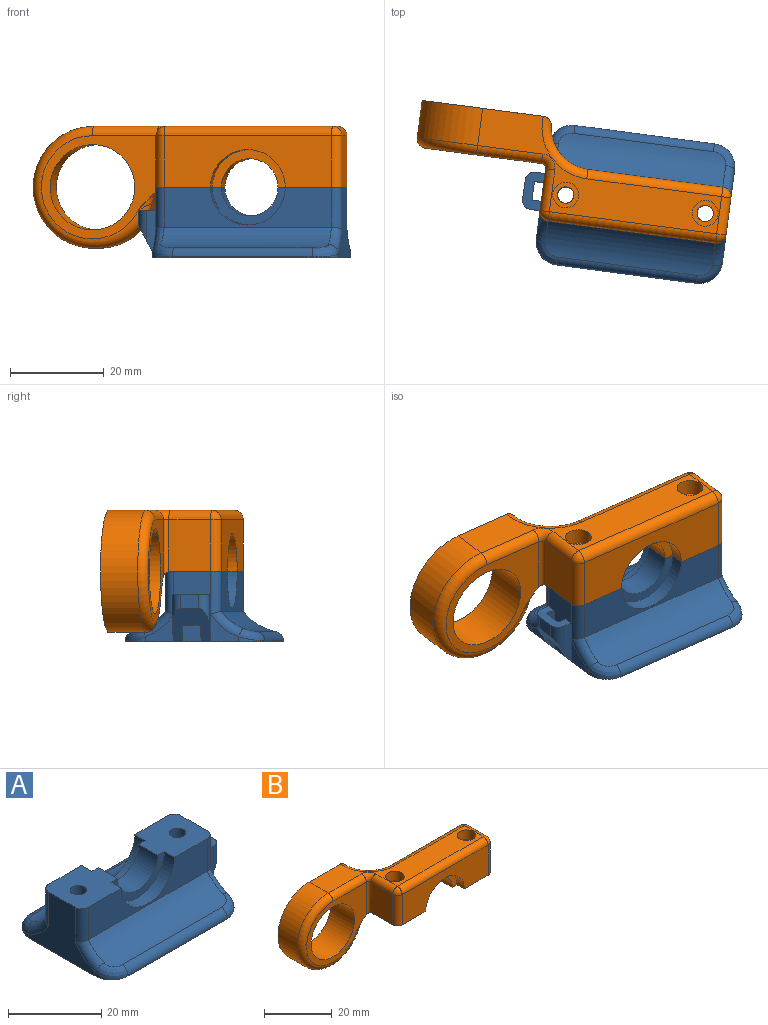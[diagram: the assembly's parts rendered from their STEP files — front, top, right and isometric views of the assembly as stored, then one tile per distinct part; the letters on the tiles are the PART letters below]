
ASSEMBLY  parts=2 mates=1
PART A: 48 faces, bbox 44.1x30x16.5 mm
  f0: plane 10x2mm, normal (0,-1,0), area 16.5mm2, adj f6,f25,f44,f45,f46
  f1: plane 10x2mm, normal (0,-1,0), area 16.5mm2, adj f2,f5,f44,f45
  f2: plane 6.5x4mm, normal (-1,0,0), area 26mm2, adj f1,f3,f44,f45
  f3: plane 10x2mm, normal (0,1,0), area 16.5mm2, adj f2,f5,f44,f45
  f4: plane 10x2mm, normal (0,1,0), area 16.5mm2, adj f7,f32,f44,f45,f47
  f5: plane 15x8mm, normal (1,0,0), area 80mm2, adj f1,f3,f10,f11,f25,f32,f44
  f6: plane 6x5.86mm, normal (1,0,0), area 17.5mm2, adj f0,f10,f24,f26
  f7: plane 6x5.86mm, normal (1,0,0), area 17.5mm2, adj f4,f10,f22,f33
  f8: cylinder r=6.1mm len=12.2mm, axis (0,1,0), area 111.1mm2, adj f11,f12,f40,f42
  f9: plane 36x8.5mm, normal (0,1,0), area 204.2mm2, adj f11,f12,f16,f32,f35,f39
  f10: plane 40x30mm, normal (0,0,-1), area 1159.3mm2, adj f5,f6,f7,f13,f14,f15,f19,f20
  f11: plane 13.9x12mm, normal (0,0,1), area 143.4mm2, adj f5,f8,f9,f18,f20,f25,f32,f39
  f12: plane 13.9x12mm, normal (0,0,1), area 143.4mm2, adj f8,f9,f13,f18,f19,f27,f35,f39
  f13: plane 20x15mm, normal (-1,0,0), area 155.1mm2, adj f10,f12,f21,f23,f27,f29,f35,f37
  f14: plane 30x0.15mm, normal (0,-1,0), area 4.6mm2, adj f10,f23,f24,f30
  f15: plane 30x0.15mm, normal (0,1,0), area 4.6mm2, adj f10,f21,f22,f36
  f16: cylinder r=11.25mm len=36mm, axis (1,0,0), area 310.8mm2, adj f9,f33,f34,f36,f37,f38
  f17: cylinder r=11.25mm len=36mm, axis (1,0,0), area 310.8mm2, adj f18,f26,f28,f29,f30,f31
  f18: plane 36x8.5mm, normal (0,-1,0), area 204.2mm2, adj f11,f12,f17,f25,f27,f41
  f19: cylinder r=1.75mm len=15mm, axis (0,0,-1), area 164.9mm2, adj f10,f12
  f20: cylinder r=1.75mm len=15mm, axis (0,0,-1), area 164.9mm2, adj f10,f11
  f21: cylinder r=5mm len=5mm, axis (0,0,-1), area 3.1mm2, adj f10,f13,f15,f38
  f22: cylinder r=5mm len=5mm, axis (0,0,1), area 3.1mm2, adj f7,f10,f15,f34
  f23: cylinder r=5mm len=5mm, axis (0,0,1), area 3.1mm2, adj f10,f13,f14,f31
  f24: cylinder r=5mm len=5mm, axis (0,0,-1), area 3.1mm2, adj f6,f10,f14,f28
  f25: cylinder r=2mm len=9.14mm, axis (0,0,-1), area 27.4mm2, adj f0,f5,f11,f18,f26
  f26: torus R=13.25mm, axis (1,0,0), area 21.1mm2, adj f6,f17,f25,f28
  f27: cylinder r=2mm len=9.14mm, axis (0,0,1), area 27.4mm2, adj f12,f13,f18,f29
  f28: bspline ~6.22x5.36mm, area 18.7mm2, adj f17,f24,f26,f30
  f29: torus R=13.25mm, axis (1,0,0), area 21.1mm2, adj f13,f17,f27,f31
  f30: cylinder r=2mm len=30mm, axis (1,0,0), area 85.2mm2, adj f14,f17,f28,f31
  f31: bspline ~6.22x6.18mm, area 18.7mm2, adj f17,f23,f29,f30
  f32: cylinder r=2mm len=9.14mm, axis (0,0,1), area 27.4mm2, adj f4,f5,f9,f11,f33
  f33: torus R=13.25mm, axis (1,0,0), area 21.1mm2, adj f7,f16,f32,f34
  f34: bspline ~6.22x6.18mm, area 18.7mm2, adj f16,f22,f33,f36
  f35: cylinder r=2mm len=9.14mm, axis (0,0,-1), area 27.4mm2, adj f9,f12,f13,f37
  f36: cylinder r=2mm len=30mm, axis (1,0,0), area 85.2mm2, adj f15,f16,f34,f38
  f37: torus R=13.25mm, axis (1,0,0), area 21.1mm2, adj f13,f16,f35,f38
  f38: bspline ~6.22x6.18mm, area 18.7mm2, adj f16,f21,f36,f37
  f39: cylinder r=8.05mm len=16.1mm, axis (0,1,0), area 78.4mm2, adj f9,f11,f12,f40
  f40: plane 16.1x8.05mm, normal (0,1,0), area 43.3mm2, adj f8,f11,f12,f39
  f41: cylinder r=8.05mm len=16.1mm, axis (0,-1,0), area 78.4mm2, adj f11,f12,f18,f42
  f42: plane 16.1x8.05mm, normal (0,-1,0), area 43.3mm2, adj f8,f11,f12,f41
  f43: plane 4x3mm, normal (1,0,0), area 12mm2, adj f44,f45,f46,f47
  f44: plane 8x4mm, normal (0,0,1), area 22.3mm2, adj f0,f1,f2,f3,f4,f5,f43,f46
  f45: plane 8x7mm, normal (0.87,0,-0.5), area 44.9mm2, adj f0,f1,f2,f3,f4,f10,f43,f46
  f46: cylinder r=2mm len=6.5mm, axis (0,0,1), area 13.4mm2, adj f0,f43,f44,f45
  f47: cylinder r=2mm len=6.5mm, axis (0,0,1), area 13.4mm2, adj f4,f43,f44,f45
PART B: 41 faces, bbox 70.1x23.2x29.1 mm
  f0: plane 53x20mm, normal (0,0,1), area 356.4mm2, adj f7,f9,f21,f22,f25,f28,f31,f32
  f1: cylinder r=1.75mm len=9.5mm, axis (0,0,1), area 104.5mm2, adj f4,f40
  f2: cylinder r=1.75mm len=9.5mm, axis (0,0,1), area 104.5mm2, adj f6,f37
  f3: cylinder r=6.1mm len=12.2mm, axis (0,-1,0), area 111.1mm2, adj f4,f6,f16,f18
  f4: plane 13.9x12mm, normal (0,0,-1), area 143.4mm2, adj f1,f3,f5,f10,f12,f15,f16,f17
  f5: plane 11x8mm, normal (1,0,0), area 88mm2, adj f4,f23,f25,f26
  f6: plane 15x13.9mm, normal (0,0,-1), area 146.9mm2, adj f2,f3,f10,f12,f13,f14,f15,f16
  f7: plane 26.05x26mm, normal (0,1,0), area 308mm2, adj f0,f8,f9,f20,f35
  f8: cylinder r=9.1mm len=18.2mm, axis (0,1,0), area 571.8mm2, adj f7,f11
  f9: cylinder r=13mm len=26mm, axis (0,1,0), area 460.8mm2, adj f0,f7,f34,f35
  f10: plane 36x11mm, normal (0,-1,0), area 294.2mm2, adj f4,f6,f17,f26,f28,f29
  f11: plane 25.99x22.99mm, normal (0,-1,0), area 186.1mm2, adj f8,f19,f33,f34,f36
  f12: plane 29x11mm, normal (0,1,0), area 217.2mm2, adj f4,f6,f13,f15,f22,f23
  f13: cylinder r=9mm len=11.54mm, axis (0,0,1), area 148mm2, adj f6,f12,f20,f21,f35
  f14: plane 11.39x9.19mm, normal (-1,0,0), area 99.1mm2, adj f6,f19,f29,f31,f36
  f15: cylinder r=8.05mm len=16.1mm, axis (0,1,0), area 78.4mm2, adj f4,f6,f12,f16
  f16: plane 16.1x8.05mm, normal (0,1,0), area 43.3mm2, adj f3,f4,f6,f15
  f17: cylinder r=8.05mm len=16.1mm, axis (0,-1,0), area 78.4mm2, adj f4,f6,f10,f18
  f18: plane 16.1x8.05mm, normal (0,-1,0), area 43.3mm2, adj f3,f4,f6,f17
  f19: cylinder r=1mm len=11.83mm, axis (0,0,1), area 18.1mm2, adj f11,f14,f32,f36
  f20: cylinder r=2mm len=15.36mm, axis (0,0,1), area 39.8mm2, adj f7,f13,f21,f35
  f21: torus R=11mm, axis (0,0,1), area 49mm2, adj f0,f13,f20,f22
  f22: cylinder r=2mm len=29mm, axis (-1,0,0), area 91.1mm2, adj f0,f12,f21,f24
  f23: cylinder r=2mm len=11mm, axis (0,0,1), area 34.6mm2, adj f4,f5,f12,f24
  f24: sphere r=2mm, area 4mm2, adj f22,f23,f25
  f25: cylinder r=2mm len=8mm, axis (0,1,0), area 25.1mm2, adj f0,f5,f24,f27
  f26: cylinder r=2mm len=11mm, axis (0,0,-1), area 34.6mm2, adj f4,f5,f10,f27
  f27: sphere r=2mm, area 6.3mm2, adj f25,f26,f28
  f28: cylinder r=2mm len=36mm, axis (1,0,0), area 113.1mm2, adj f0,f10,f27,f30
  f29: cylinder r=2mm len=11mm, axis (0,0,-1), area 34.6mm2, adj f6,f10,f14,f30
  f30: sphere r=2mm, area 6.3mm2, adj f28,f29,f31
  f31: cylinder r=2mm len=9mm, axis (0,-1,0), area 28.3mm2, adj f0,f14,f30,f32
  f32: torus R=3mm, axis (0,0,1), area 8.5mm2, adj f0,f19,f31,f33
  f33: cylinder r=2mm len=14mm, axis (1,0,0), area 44mm2, adj f0,f11,f32,f34
  f34: torus R=11mm, axis (0,-1,0), area 167.3mm2, adj f9,f11,f33,f36
  f35: cylinder r=5mm len=8mm, axis (0,1,0), area 40.2mm2, adj f6,f7,f9,f13,f20,f36
  f36: bspline ~8.37x7.31mm, area 21.1mm2, adj f6,f11,f14,f19,f34,f35
  f37: plane 5.5x5.5mm, normal (0,0,1), area 14.1mm2, adj f2,f38
  f38: cylinder r=2.75mm len=5.5mm, axis (0,0,1), area 60.5mm2, adj f0,f37
  f39: cylinder r=2.75mm len=5.5mm, axis (0,0,1), area 60.5mm2, adj f0,f40
  f40: plane 5.5x5.5mm, normal (0,0,1), area 14.1mm2, adj f1,f39
PLACE A rot(axis=(0,0,1),172.5deg) t=(-32.88,18.93,6.61)mm
PLACE B rot(axis=(0,0,-1),7.5deg) t=(-30.79,34.79,21.61)mm
MATE parallel B.f1 <-> A.f19  axis (0,0,-1) through (-18.01,16.97,21.61)mm
